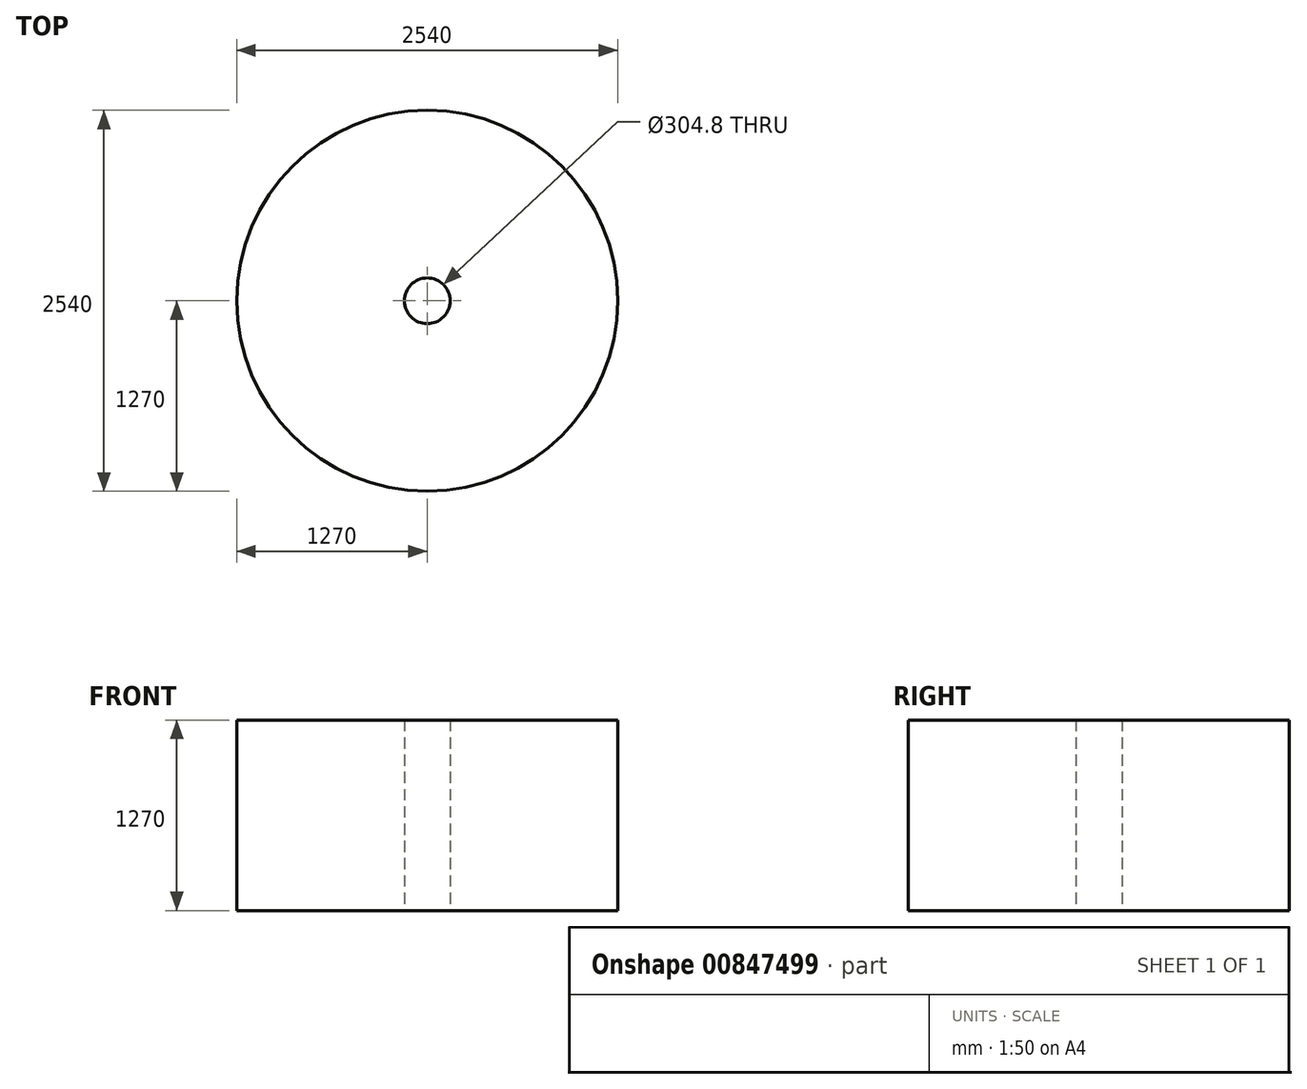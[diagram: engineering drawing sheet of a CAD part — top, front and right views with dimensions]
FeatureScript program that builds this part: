
annotation { "Feature Type Name" : "Feature", "Feature Type Description" : "" }
export const myFeature = defineFeature(function(context is Context, id is Id, definition is map)
    precondition{}
    {
        {
            var Q0;
            Q0=qCreatedBy(makeId("Top.planeOp"),FACE);
            var sketch = newSketch(context, id + "F0", { "sketchPlane" : qUnion([Q0])});
            skCircle(sketch, "E0", {"center": v(0, 0) * mm, "radius": 1270 * mm});
            skCircle(sketch, "E1", {"center": v(0, 0) * mm, "radius": 152.4 * mm});
            skSolve(sketch);
        }
        {
            var Q0;
            Q0=makeQuery(id+"F0.imprint","IMPRINT",FACE,{"disambiguationData":[TD([[makeQuery(id+"F0.imprint","IMPRINT",EDGE,{"derivedFrom":sQuery(id+"F0.wireOp",EDGE,"E0")}),1.0]])]});
            extrude(context, id + "F1", {"entities" : qUnion([Q0]), "depth" : 1270 * mm, "offsetDistance" : 25.4 * mm});
        }
    });
